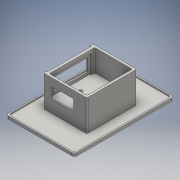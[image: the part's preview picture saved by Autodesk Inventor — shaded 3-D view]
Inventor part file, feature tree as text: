
AUTODESK INVENTOR PART (.ipt)
format: ipt  version: 2016 (Build 200138000, 138)  size: 257,024 bytes
history: native  units: mm
features: extrude x10, sketch x10
ambient origin geometry x8: Origin, YZ Plane, XZ Plane, XY Plane, X Axis, Y Axis, Z Axis, Center Point
bodies: Solid1 (feature_tree)
feature tree (20):
  extrude  "xyAttach"  Depth=159.5mm
  extrude  "spillExtrusion"  Depth=79.75mm
  extrude  "chamberWallExtrusion"  Depth=3.0mm TaperAngle=0.0deg
  extrude  "chamberInteriorExtrusion"  Depth=4.0mm
  extrude  "rectCoverSlipMountExtrusion"  Depth=2.0mm
  extrude  "rectCoverSlipWindow"  Depth=2.0mm
  extrude  "illObjExtrusion"  Depth=70.0mm
  extrude  "viewingWindowCoverslipMount"  Depth=80.0mm
  extrude  "viewingWindowExt"  Depth=2.0mm
  extrude  "sampleMountExt"  Depth=2.0mm
  sketch  "Sketch1"  dims[d0=109.5mm d1=159.5mm]
  sketch  "Sketch2"  dims[d2=54.75mm d3=79.75mm]
  sketch  "Sketch3"  dims[d4=4.0mm d5=3.0mm d6=0.0mm]
  sketch  "Sketch4"  dims[d7=4.0mm d8=4.0mm]
  sketch  "Sketch5"  dims[d9=2.0mm d10=2.0mm]
  sketch  "Sketch6"  dims[d11=2.0mm d12=2.0mm]
  sketch  "Sketch7"  dims[d13=2.0mm d14=0.0mm d15=70.0mm]
  sketch  "Sketch8"  dims[d16=35.0mm d17=80.0mm]
  sketch  "Sketch9"  dims[d18=40.0mm d19=2.0mm]
  sketch  "Sketch10"  dims[d20=50.0mm d21=0.0mm d22=2.0mm d23=3.5mm d24=3.5mm d25=3.5mm d26=6.0mm d27=35.5mm d28=0.0mm d29=62.5mm d30=30.0mm d31=31.25mm d32=42.5mm d33=2.0mm d34=0.0mm d35=55.0mm d36=20.0mm d37=37.5mm d38=27.5mm d39=2.0mm d40=0.0mm d41=70.0mm d42=35.0mm d43=2.0mm d44=0.0mm d46=45.0mm d47=25.0mm d48=40.0mm d50=2.0mm d51=0.0mm d52=35.0mm d53=17.0mm d55=36.0mm d56=2.0mm d57=0.0mm d58=5.65mm d59=5.65mm d60=5.65mm d61=5.65mm d62=5.65mm d63=15.0mm d64=15.0mm d65=15.0mm d66=15.0mm d67=2.0mm d68=0.0mm d69=2.5mm d71=5.0mm]
